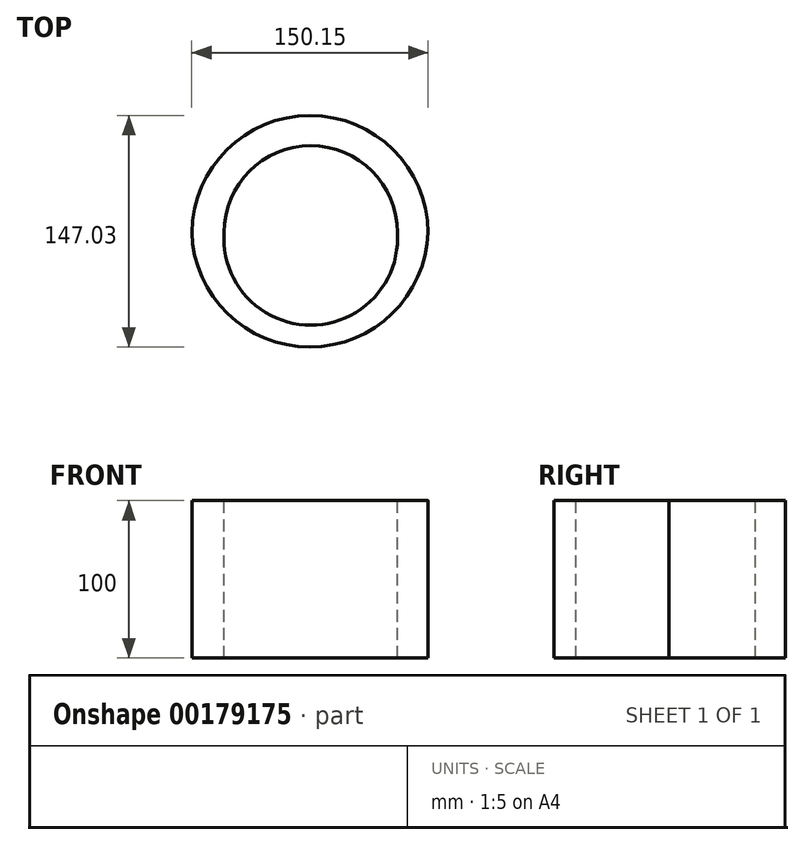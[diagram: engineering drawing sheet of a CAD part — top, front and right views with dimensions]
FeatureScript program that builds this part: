
annotation { "Feature Type Name" : "Feature", "Feature Type Description" : "" }
export const myFeature = defineFeature(function(context is Context, id is Id, definition is map)
    precondition{}
    {
        {
            var Q0;
            Q0=qCreatedBy(makeId("Top.planeOp"),FACE);
            var sketch = newSketch(context, id + "F0", { "sketchPlane" : qUnion([Q0])});
            skArc(sketch, "E0", {"start": v(74.86, 0) * mm, "mid": v(-0.14, 74.17) * mm, "end": v(-75.14, 0) * mm});
            skArc(sketch, "E1", {"start": v(55.23, 0) * mm, "mid": v(0.23, 55) * mm, "end": v(-54.77, 0) * mm});
            skSolve(sketch);
        }
        {
            var Q0;
            Q0=sQuery(id+"F0.wireOp",EDGE,"E0");
            var Q1;
            Q1=sQuery(id+"F0.wireOp",EDGE,"E1");
            extrude(context, id + "F1", {"bodyType" : ToolBodyType.SURFACE, "surfaceEntities" : qUnion([Q0, Q1]), "depth" : 100 * mm});
        }
        {
            var Q0;
            Q0=qCreatedBy(makeId("Top.planeOp"),FACE);
            var sketch = newSketch(context, id + "F2", { "sketchPlane" : qUnion([Q0])});
            skArc(sketch, "E2", {"start": v(-75.29, 0) * mm, "mid": v(-0.29, -72.86) * mm, "end": v(74.71, 0) * mm});
            skArc(sketch, "E3", {"start": v(-54.75, 0) * mm, "mid": v(0.25, -58.95) * mm, "end": v(55.25, 0) * mm});
            skLineSegment(sketch, "E4", {"start": v(-75.29, 0) * mm, "end": v(74.71, 0) * mm});
            skLineSegment(sketch, "E5", {"start": v(-75.12, -3.29) * mm, "end": v(74.55, -3.29) * mm});
            skSolve(sketch);
        }
        {
            var Q0;
            Q0=sQuery(id+"F2.wireOp",EDGE,"E2");
            var Q1;
            Q1=sQuery(id+"F2.wireOp",EDGE,"E3");
            extrude(context, id + "F3", {"bodyType" : ToolBodyType.SURFACE, "surfaceEntities" : qUnion([Q0, Q1]), "depth" : 100 * mm});
        }
    });
